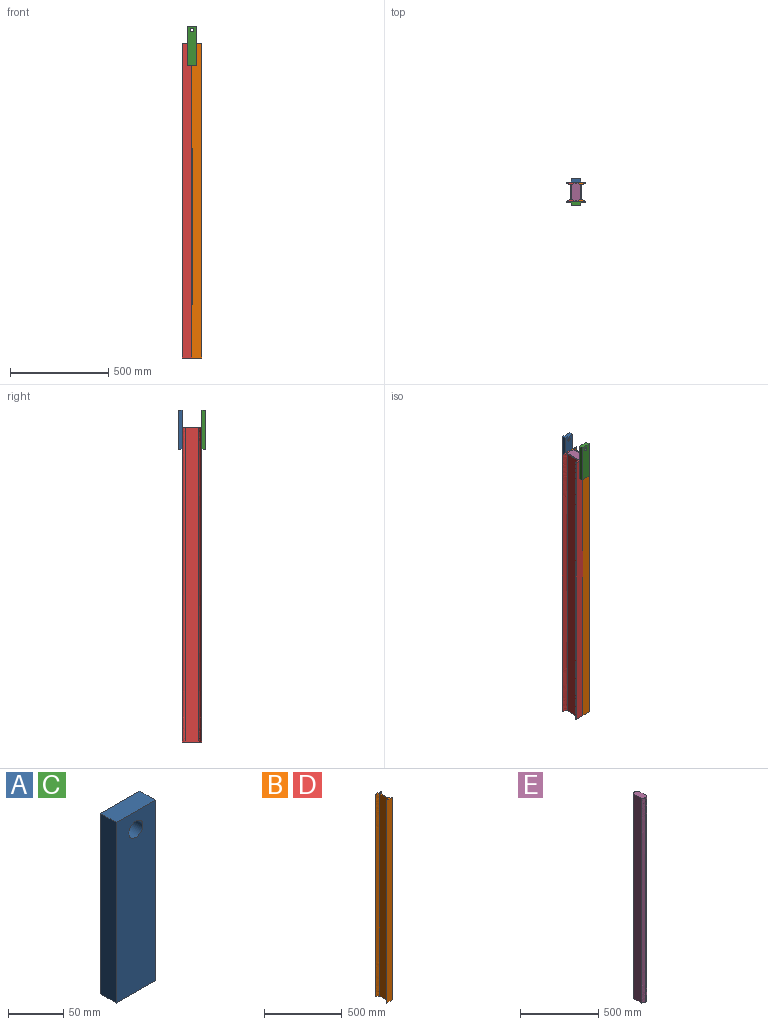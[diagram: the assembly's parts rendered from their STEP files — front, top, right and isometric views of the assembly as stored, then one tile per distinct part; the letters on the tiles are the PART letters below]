
ASSEMBLY  parts=5 mates=4
PART A: 7 faces, bbox 50x20x200 mm
  f0: plane 50x20mm, normal (0,0,-1), area 1000mm2, adj f1,f4,f5,f6
  f1: plane 200x20mm, normal (1,0,0), area 4000mm2, adj f0,f2,f5,f6
  f2: plane 50x20mm, normal (0,0,1), area 1000mm2, adj f1,f4,f5,f6
  f3: cylinder r=9mm len=20mm, axis (0,1,0), area 1131mm2, adj f5,f6
  f4: plane 200x20mm, normal (-1,0,0), area 4000mm2, adj f0,f2,f5,f6
  f5: plane 200x50mm, normal (0,-1,0), area 9745.5mm2, adj f0,f1,f2,f3,f4
  f6: plane 200x50mm, normal (0,1,0), area 9745.5mm2, adj f0,f1,f2,f3,f4
PART B: 12 faces, bbox 50x100x1600 mm
  f0: extruded ~1600x0mm, area 1.6mm2, adj f1,f9,f10,f11
  f1: plane 1600x50mm, normal (0,1,0), area 80000mm2, adj f0,f2,f10,f11
  f2: extruded ~1600x22.5mm, area 45356.5mm2, adj f1,f3,f10,f11
  f3: plane 1600x70.75mm, normal (-1,0,0), area 113200mm2, adj f2,f4,f10,f11
  f4: extruded ~1600x22.5mm, area 45356.5mm2, adj f3,f5,f10,f11
  f5: plane 1600x50mm, normal (0,-1,0), area 80000mm2, adj f4,f6,f10,f11
  f6: extruded ~1600x0mm, area 1.6mm2, adj f5,f7,f10,f11
  f7: extruded ~1600x22.5mm, area 45354.9mm2, adj f6,f8,f10,f11
  f8: plane 1600x70.75mm, normal (1,0,0), area 113200mm2, adj f7,f9,f10,f11
  f9: extruded ~1600x22.5mm, area 45354.9mm2, adj f0,f8,f10,f11
  f10: plane 100x50mm, normal (0,0,1), area 1141.3mm2, adj f0,f1,f2,f3,f4,f5,f6,f7
  f11: plane 100x50mm, normal (0,0,-1), area 1141.3mm2, adj f0,f1,f2,f3,f4,f5,f6,f7
PART C: same geometry as A
PART D: same geometry as B
PART E: 8 faces, bbox 45x100x1600 mm
  f0: extruded ~1600x22.5mm, area 45354.9mm2, adj f1,f5,f6,f7
  f1: extruded ~1600x22.5mm, area 45354.9mm2, adj f0,f2,f6,f7
  f2: plane 1600x70.75mm, normal (1,0,0), area 113200mm2, adj f1,f3,f6,f7
  f3: extruded ~1600x22.5mm, area 45354.9mm2, adj f2,f4,f6,f7
  f4: extruded ~1600x22.5mm, area 45354.9mm2, adj f3,f5,f6,f7
  f5: plane 1600x70.75mm, normal (-1,0,0), area 113200mm2, adj f0,f4,f6,f7
  f6: plane 100x45mm, normal (0,0,1), area 3858.7mm2, adj f0,f1,f2,f3,f4,f5
  f7: plane 100x45mm, normal (0,0,-1), area 3858.7mm2, adj f0,f1,f2,f3,f4,f5
PLACE A t=(0,70,1490)mm
PLACE B t=(0,-50,0)mm
PLACE C t=(0,-50,1490)mm
PLACE D t=(-50,-50,0)mm
PLACE E t=(-50,-50,0)mm
MATE fastened D.f8 <-> E.f5  axis (1,0,0) through (-22.5,0,800)mm
MATE fastened C.f6 <-> B.f5  axis (0,1,0) through (0,-50,1490)mm
MATE fastened B.f3 <-> E.f2  axis (-1,0,0) through (22.5,0,800)mm
MATE fastened A.f5 <-> B.f1  axis (0,-1,0) through (0,50,1490)mm
